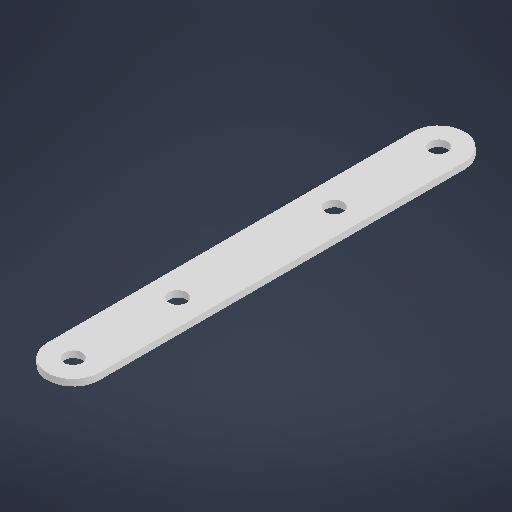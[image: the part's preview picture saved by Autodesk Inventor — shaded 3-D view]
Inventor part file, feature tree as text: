
AUTODESK INVENTOR PART (.ipt)
format: ipt  version: 2025.2 (Build 292293000, 293)  size: 198,144 bytes
history: native  units: in
note: dims shown in document units (in); Inventor stores cm internally (conversion verified against a paired STEP export)
features: extrude x1, sketch x1
ambient origin geometry x8: Origin, YZ Plane, XZ Plane, XY Plane, X Axis, Y Axis, Z Axis, Center Point
bodies: Solid1 (feature_tree)
feature tree (2):
  extrude  "Extrusion1"  Depth=0.0625in
  sketch  "Sketch1"  dims[d0=1.0in d1=1.5in d2=1.0in d3=1.0in d4=0.172in d5=0.172in d6=0.172in d8=0.5in d10=0.0625in d11=0.0in d12=0.172in]
